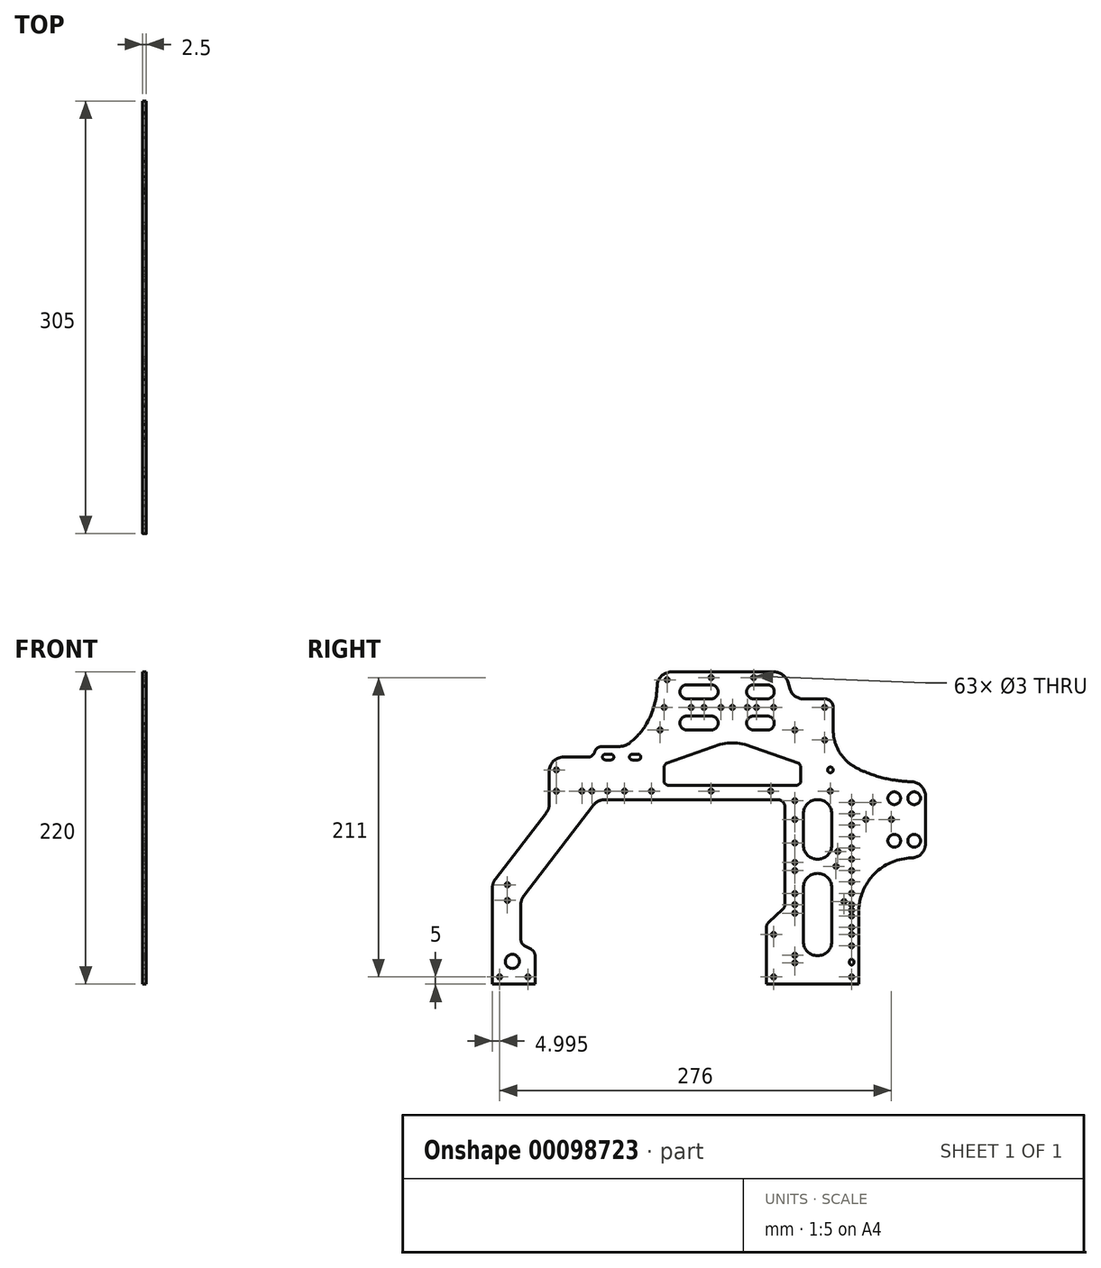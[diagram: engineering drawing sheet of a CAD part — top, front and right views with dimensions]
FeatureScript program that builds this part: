
annotation { "Feature Type Name" : "Feature", "Feature Type Description" : "" }
export const myFeature = defineFeature(function(context is Context, id is Id, definition is map)
    precondition{}
    {
        {
            var Q0;
            Q0=qCreatedBy(makeId("Right.planeOp"),FACE);
            var sketch = newSketch(context, id + "F0", { "sketchPlane" : qUnion([Q0])});
            skLineSegment(sketch, "E0", {"start": v(13.27, 60) * mm, "end": v(19.72, 60) * mm});
            skLineSegment(sketch, "E1", {"start": v(19.72, 60) * mm, "end": v(25.1, 59.07) * mm});
            skLineSegment(sketch, "E2", {"start": v(25.1, 59.07) * mm, "end": v(63.17, 45.47) * mm});
            skLineSegment(sketch, "E3", {"start": v(63.17, 45.47) * mm, "end": v(64.5, 43.6) * mm});
            skLineSegment(sketch, "E4", {"start": v(64.5, 43.6) * mm, "end": v(64.5, 32) * mm});
            skLineSegment(sketch, "E5", {"start": v(64.5, 32) * mm, "end": v(62.5, 30) * mm});
            skLineSegment(sketch, "E6", {"start": v(62.5, 30) * mm, "end": v(-29.5, 30) * mm});
            skLineSegment(sketch, "E7", {"start": v(-29.5, 30) * mm, "end": v(-31.5, 32) * mm});
            skLineSegment(sketch, "E8", {"start": v(-31.5, 32) * mm, "end": v(-31.5, 43.6) * mm});
            skLineSegment(sketch, "E9", {"start": v(-31.5, 43.6) * mm, "end": v(-30.18, 45.47) * mm});
            skLineSegment(sketch, "E10", {"start": v(-30.18, 45.47) * mm, "end": v(7.89, 59.07) * mm});
            skLineSegment(sketch, "E11", {"start": v(7.89, 59.07) * mm, "end": v(13.27, 60) * mm});
            skCircle(sketch, "E12", {"center": v(-138.5, -94) * mm, "radius": 5 * mm});
            skCircle(sketch, "E13", {"center": v(-147.5, -105) * mm, "radius": 1.5 * mm});
            skCircle(sketch, "E14", {"center": v(-127.5, -105) * mm, "radius": 1.5 * mm});
            skCircle(sketch, "E15", {"center": v(-142, -51) * mm, "radius": 1.5 * mm});
            skCircle(sketch, "E16", {"center": v(-142, -40) * mm, "radius": 1.5 * mm});
            skCircle(sketch, "E17", {"center": v(-107.5, 26) * mm, "radius": 1.5 * mm});
            skCircle(sketch, "E18", {"center": v(-107.5, 41) * mm, "radius": 1.5 * mm});
            skCircle(sketch, "E19", {"center": v(-89.5, 26) * mm, "radius": 1.5 * mm});
            skCircle(sketch, "E20", {"center": v(-82.5, 26) * mm, "radius": 1.5 * mm});
            skCircle(sketch, "E21", {"center": v(-71.5, 26) * mm, "radius": 1.5 * mm});
            skArc(sketch, "E22", {"start": v(-75, 50) * mm, "mid": v(-74.42, 48.59) * mm, "end": v(-73, 48) * mm});
            skLineSegment(sketch, "E23", {"start": v(-73, 48) * mm, "end": v(-69, 48) * mm});
            skArc(sketch, "E24", {"start": v(-69, 48) * mm, "mid": v(-67.6, 48.59) * mm, "end": v(-67, 50) * mm});
            skArc(sketch, "E25", {"start": v(-67, 50) * mm, "mid": v(-67.6, 51.41) * mm, "end": v(-69, 52) * mm});
            skLineSegment(sketch, "E26", {"start": v(-69, 52) * mm, "end": v(-73, 52) * mm});
            skArc(sketch, "E27", {"start": v(-73, 52) * mm, "mid": v(-74.42, 51.41) * mm, "end": v(-75, 50) * mm});
            skArc(sketch, "E28", {"start": v(-56, 50) * mm, "mid": v(-55.42, 48.59) * mm, "end": v(-54, 48) * mm});
            skLineSegment(sketch, "E29", {"start": v(-54, 48) * mm, "end": v(-50, 48) * mm});
            skArc(sketch, "E30", {"start": v(-50, 48) * mm, "mid": v(-48.6, 48.59) * mm, "end": v(-48, 50) * mm});
            skArc(sketch, "E31", {"start": v(-48, 50) * mm, "mid": v(-48.6, 51.41) * mm, "end": v(-50, 52) * mm});
            skLineSegment(sketch, "E32", {"start": v(-50, 52) * mm, "end": v(-54, 52) * mm});
            skArc(sketch, "E33", {"start": v(-54, 52) * mm, "mid": v(-55.42, 51.41) * mm, "end": v(-56, 50) * mm});
            skCircle(sketch, "E34", {"center": v(-40.5, 26) * mm, "radius": 1.5 * mm});
            skCircle(sketch, "E35", {"center": v(1.5, 26) * mm, "radius": 1.5 * mm});
            skCircle(sketch, "E36", {"center": v(43.5, 26) * mm, "radius": 1.5 * mm});
            skCircle(sketch, "E37", {"center": v(60.5, 6) * mm, "radius": 1.5 * mm});
            skCircle(sketch, "E38", {"center": v(60.5, -10.5) * mm, "radius": 1.5 * mm});
            skLineSegment(sketch, "E39", {"start": v(66.5, 10) * mm, "end": v(66.5, -12) * mm});
            skArc(sketch, "E40", {"start": v(66.5, -12) * mm, "mid": v(69.42, -19.07) * mm, "end": v(76.5, -22) * mm});
            skArc(sketch, "E41", {"start": v(76.5, -22) * mm, "mid": v(83.57, -19.07) * mm, "end": v(86.5, -12) * mm});
            skLineSegment(sketch, "E42", {"start": v(86.5, -12) * mm, "end": v(86.5, 10) * mm});
            skArc(sketch, "E43", {"start": v(86.5, 10) * mm, "mid": v(83.57, 17.07) * mm, "end": v(76.5, 20) * mm});
            skArc(sketch, "E44", {"start": v(76.5, 20) * mm, "mid": v(69.42, 17.07) * mm, "end": v(66.5, 10) * mm});
            skLineSegment(sketch, "E45", {"start": v(66.5, -42) * mm, "end": v(66.5, -80) * mm});
            skArc(sketch, "E46", {"start": v(66.5, -80) * mm, "mid": v(69.42, -87.07) * mm, "end": v(76.5, -90) * mm});
            skArc(sketch, "E47", {"start": v(76.5, -90) * mm, "mid": v(83.57, -87.07) * mm, "end": v(86.5, -80) * mm});
            skLineSegment(sketch, "E48", {"start": v(86.5, -80) * mm, "end": v(86.5, -42) * mm});
            skArc(sketch, "E49", {"start": v(86.5, -42) * mm, "mid": v(83.57, -34.93) * mm, "end": v(76.5, -32) * mm});
            skArc(sketch, "E50", {"start": v(76.5, -32) * mm, "mid": v(69.42, -34.93) * mm, "end": v(66.5, -42) * mm});
            skCircle(sketch, "E51", {"center": v(130.5, -9) * mm, "radius": 4.5 * mm});
            skCircle(sketch, "E52", {"center": v(144.5, -9) * mm, "radius": 4.5 * mm});
            skCircle(sketch, "E53", {"center": v(130.5, 21) * mm, "radius": 4.5 * mm});
            skCircle(sketch, "E54", {"center": v(144.5, 21) * mm, "radius": 4.5 * mm});
            skArc(sketch, "E55", {"start": v(-20.5, 74) * mm, "mid": v(-19.04, 70.46) * mm, "end": v(-15.5, 69) * mm});
            skLineSegment(sketch, "E56", {"start": v(-15.5, 69) * mm, "end": v(1.5, 69) * mm});
            skArc(sketch, "E57", {"start": v(1.5, 69) * mm, "mid": v(5.03, 70.46) * mm, "end": v(6.5, 74) * mm});
            skArc(sketch, "E58", {"start": v(6.5, 74) * mm, "mid": v(5.03, 77.54) * mm, "end": v(1.5, 79) * mm});
            skLineSegment(sketch, "E59", {"start": v(1.5, 79) * mm, "end": v(-15.5, 79) * mm});
            skArc(sketch, "E60", {"start": v(-15.5, 79) * mm, "mid": v(-19.04, 77.54) * mm, "end": v(-20.5, 74) * mm});
            skArc(sketch, "E61", {"start": v(-20.5, 96) * mm, "mid": v(-19.04, 92.46) * mm, "end": v(-15.5, 91) * mm});
            skLineSegment(sketch, "E62", {"start": v(-15.5, 91) * mm, "end": v(1.5, 91) * mm});
            skArc(sketch, "E63", {"start": v(1.5, 91) * mm, "mid": v(5.03, 92.46) * mm, "end": v(6.5, 96) * mm});
            skArc(sketch, "E64", {"start": v(6.5, 96) * mm, "mid": v(5.03, 99.54) * mm, "end": v(1.5, 101) * mm});
            skLineSegment(sketch, "E65", {"start": v(1.5, 101) * mm, "end": v(-15.5, 101) * mm});
            skArc(sketch, "E66", {"start": v(-15.5, 101) * mm, "mid": v(-19.04, 99.54) * mm, "end": v(-20.5, 96) * mm});
            skArc(sketch, "E67", {"start": v(26.5, 96) * mm, "mid": v(27.96, 92.46) * mm, "end": v(31.5, 91) * mm});
            skLineSegment(sketch, "E68", {"start": v(31.5, 91) * mm, "end": v(41, 91) * mm});
            skArc(sketch, "E69", {"start": v(41, 91) * mm, "mid": v(44.53, 92.46) * mm, "end": v(46, 96) * mm});
            skArc(sketch, "E70", {"start": v(46, 96) * mm, "mid": v(44.53, 99.54) * mm, "end": v(41, 101) * mm});
            skLineSegment(sketch, "E71", {"start": v(41, 101) * mm, "end": v(31.5, 101) * mm});
            skArc(sketch, "E72", {"start": v(31.5, 101) * mm, "mid": v(27.96, 99.54) * mm, "end": v(26.5, 96) * mm});
            skArc(sketch, "E73", {"start": v(26.5, 74) * mm, "mid": v(27.96, 70.46) * mm, "end": v(31.5, 69) * mm});
            skLineSegment(sketch, "E74", {"start": v(31.5, 69) * mm, "end": v(41, 69) * mm});
            skArc(sketch, "E75", {"start": v(41, 69) * mm, "mid": v(44.53, 70.46) * mm, "end": v(46, 74) * mm});
            skArc(sketch, "E76", {"start": v(46, 74) * mm, "mid": v(44.53, 77.54) * mm, "end": v(41, 79) * mm});
            skLineSegment(sketch, "E77", {"start": v(41, 79) * mm, "end": v(31.5, 79) * mm});
            skArc(sketch, "E78", {"start": v(31.5, 79) * mm, "mid": v(27.96, 77.54) * mm, "end": v(26.5, 74) * mm});
            skCircle(sketch, "E79", {"center": v(-34.5, 69) * mm, "radius": 1.5 * mm});
            skCircle(sketch, "E80", {"center": v(-31.5, 85) * mm, "radius": 1.5 * mm});
            skCircle(sketch, "E81", {"center": v(-29.5, 104.5) * mm, "radius": 1.5 * mm});
            skCircle(sketch, "E82", {"center": v(-12.5, 85) * mm, "radius": 1.5 * mm});
            skCircle(sketch, "E83", {"center": v(-3.5, 85) * mm, "radius": 1.5 * mm});
            skCircle(sketch, "E84", {"center": v(8.5, 85) * mm, "radius": 1.5 * mm});
            skCircle(sketch, "E85", {"center": v(16.5, 85) * mm, "radius": 1.5 * mm});
            skCircle(sketch, "E86", {"center": v(27, 85) * mm, "radius": 1.5 * mm});
            skCircle(sketch, "E87", {"center": v(33.5, 85) * mm, "radius": 1.5 * mm});
            skCircle(sketch, "E88", {"center": v(45.5, 85) * mm, "radius": 1.5 * mm});
            skCircle(sketch, "E89", {"center": v(1.5, 106) * mm, "radius": 1.5 * mm});
            skCircle(sketch, "E90", {"center": v(31.5, 106) * mm, "radius": 1.5 * mm});
            skCircle(sketch, "E91", {"center": v(81.5, 85) * mm, "radius": 1.5 * mm});
            skCircle(sketch, "E92", {"center": v(60.5, 69) * mm, "radius": 1.5 * mm});
            skCircle(sketch, "E93", {"center": v(60.5, -24.25) * mm, "radius": 1.5 * mm});
            skCircle(sketch, "E94", {"center": v(60.5, -30) * mm, "radius": 1.5 * mm});
            skCircle(sketch, "E95", {"center": v(60.5, 19.25) * mm, "radius": 1.5 * mm});
            skCircle(sketch, "E96", {"center": v(60.5, -46.25) * mm, "radius": 1.5 * mm});
            skCircle(sketch, "E97", {"center": v(60.5, -54) * mm, "radius": 1.5 * mm});
            skCircle(sketch, "E98", {"center": v(60.5, -60) * mm, "radius": 1.5 * mm});
            skCircle(sketch, "E99", {"center": v(45.5, -75) * mm, "radius": 1.5 * mm});
            skCircle(sketch, "E100", {"center": v(45.5, -105) * mm, "radius": 1.5 * mm});
            skCircle(sketch, "E101", {"center": v(60.5, -89.75) * mm, "radius": 1.5 * mm});
            skCircle(sketch, "E102", {"center": v(60.5, -95) * mm, "radius": 1.5 * mm});
            skCircle(sketch, "E103", {"center": v(100.5, -105) * mm, "radius": 1.5 * mm});
            skCircle(sketch, "E104", {"center": v(85.5, 26) * mm, "radius": 1.5 * mm});
            skCircle(sketch, "E105", {"center": v(85.5, 41) * mm, "radius": 2 * mm});
            skCircle(sketch, "E106", {"center": v(100.5, 18) * mm, "radius": 1.5 * mm});
            skCircle(sketch, "E107", {"center": v(100.5, 10) * mm, "radius": 1.5 * mm});
            skCircle(sketch, "E108", {"center": v(100.5, 2) * mm, "radius": 1.5 * mm});
            skCircle(sketch, "E109", {"center": v(110.5, 6) * mm, "radius": 1.5 * mm});
            skCircle(sketch, "E110", {"center": v(115.5, 18) * mm, "radius": 1.5 * mm});
            skCircle(sketch, "E111", {"center": v(128.5, 6) * mm, "radius": 1.5 * mm});
            skCircle(sketch, "E112", {"center": v(100.5, -6) * mm, "radius": 1.5 * mm});
            skCircle(sketch, "E113", {"center": v(100.5, -14) * mm, "radius": 1.5 * mm});
            skCircle(sketch, "E114", {"center": v(90.75, -16.5) * mm, "radius": 1.5 * mm});
            skCircle(sketch, "E115", {"center": v(89.5, -27) * mm, "radius": 1.5 * mm});
            skCircle(sketch, "E116", {"center": v(100.5, -22) * mm, "radius": 1.5 * mm});
            skCircle(sketch, "E117", {"center": v(100.5, -30) * mm, "radius": 1.5 * mm});
            skCircle(sketch, "E118", {"center": v(100.5, -38) * mm, "radius": 1.5 * mm});
            skCircle(sketch, "E119", {"center": v(100.5, -54) * mm, "radius": 1.5 * mm});
            skCircle(sketch, "E120", {"center": v(95.12, -51.87) * mm, "radius": 1.5 * mm});
            skCircle(sketch, "E121", {"center": v(100.5, -46) * mm, "radius": 1.5 * mm});
            skCircle(sketch, "E122", {"center": v(100.5, -58) * mm, "radius": 1.5 * mm});
            skCircle(sketch, "E123", {"center": v(100.5, -62) * mm, "radius": 1.5 * mm});
            skCircle(sketch, "E124", {"center": v(100.5, -70) * mm, "radius": 1.5 * mm});
            skCircle(sketch, "E125", {"center": v(100.5, -75) * mm, "radius": 1.5 * mm});
            skCircle(sketch, "E126", {"center": v(100.5, -83) * mm, "radius": 1.5 * mm});
            skLineSegment(sketch, "E127", {"start": v(99, -94) * mm, "end": v(99, -95) * mm});
            skArc(sketch, "E128", {"start": v(99, -95) * mm, "mid": v(99.43, -96.06) * mm, "end": v(100.5, -96.5) * mm});
            skArc(sketch, "E129", {"start": v(100.5, -96.5) * mm, "mid": v(101.56, -96.06) * mm, "end": v(102, -95) * mm});
            skLineSegment(sketch, "E130", {"start": v(102, -95) * mm, "end": v(102, -94) * mm});
            skArc(sketch, "E131", {"start": v(102, -94) * mm, "mid": v(101.56, -92.94) * mm, "end": v(100.5, -92.5) * mm});
            skArc(sketch, "E132", {"start": v(100.5, -92.5) * mm, "mid": v(99.43, -92.94) * mm, "end": v(99, -94) * mm});
            skLineSegment(sketch, "E133", {"start": v(105.5, -58) * mm, "end": v(105.5, -110) * mm});
            skLineSegment(sketch, "E134", {"start": v(105.5, -110) * mm, "end": v(40.5, -110) * mm});
            skLineSegment(sketch, "E135", {"start": v(40.5, -110) * mm, "end": v(40.5, -70.03) * mm});
            skArc(sketch, "E136", {"start": v(40.5, -70.03) * mm, "mid": v(40.92, -68.02) * mm, "end": v(42.11, -66.35) * mm});
            skLineSegment(sketch, "E137", {"start": v(42.11, -66.35) * mm, "end": v(51.88, -57.39) * mm});
            skArc(sketch, "E138", {"start": v(51.88, -57.39) * mm, "mid": v(53.07, -55.71) * mm, "end": v(53.5, -53.7) * mm});
            skLineSegment(sketch, "E139", {"start": v(53.5, -53.7) * mm, "end": v(53.5, 15) * mm});
            skArc(sketch, "E140", {"start": v(53.5, 15) * mm, "mid": v(52.03, 18.54) * mm, "end": v(48.5, 20) * mm});
            skLineSegment(sketch, "E141", {"start": v(48.5, 20) * mm, "end": v(-73.57, 20) * mm});
            skArc(sketch, "E142", {"start": v(-73.57, 20) * mm, "mid": v(-78, 18.97) * mm, "end": v(-81.5, 16.08) * mm});
            skLineSegment(sketch, "E143", {"start": v(-81.5, 16.08) * mm, "end": v(-130.44, -47.8) * mm});
            skArc(sketch, "E144", {"start": v(-130.44, -47.8) * mm, "mid": v(-131.98, -50.68) * mm, "end": v(-132.5, -53.89) * mm});
            skLineSegment(sketch, "E145", {"start": v(-132.5, -53.89) * mm, "end": v(-132.5, -78.54) * mm});
            skArc(sketch, "E146", {"start": v(-132.5, -78.54) * mm, "mid": v(-131.8, -81.09) * mm, "end": v(-129.91, -82.92) * mm});
            skLineSegment(sketch, "E147", {"start": v(-129.91, -82.92) * mm, "end": v(-125.1, -85.58) * mm});
            skArc(sketch, "E148", {"start": v(-125.1, -85.58) * mm, "mid": v(-123.2, -87.41) * mm, "end": v(-122.5, -89.96) * mm});
            skLineSegment(sketch, "E149", {"start": v(-122.5, -89.96) * mm, "end": v(-122.5, -110) * mm});
            skLineSegment(sketch, "E150", {"start": v(-122.5, -110) * mm, "end": v(-152.5, -110) * mm});
            skLineSegment(sketch, "E151", {"start": v(-152.5, -110) * mm, "end": v(-152.5, -42.06) * mm});
            skArc(sketch, "E152", {"start": v(-152.5, -42.06) * mm, "mid": v(-151.97, -38.85) * mm, "end": v(-150.44, -35.97) * mm});
            skLineSegment(sketch, "E153", {"start": v(-150.44, -35.97) * mm, "end": v(-114.57, 10.8) * mm});
            skArc(sketch, "E154", {"start": v(-114.57, 10.8) * mm, "mid": v(-113.03, 13.68) * mm, "end": v(-112.5, 16.9) * mm});
            skLineSegment(sketch, "E155", {"start": v(-112.5, 16.9) * mm, "end": v(-112.5, 40) * mm});
            skArc(sketch, "E156", {"start": v(-112.5, 40) * mm, "mid": v(-109.58, 47.07) * mm, "end": v(-102.5, 50) * mm});
            skLineSegment(sketch, "E157", {"start": v(-102.5, 50) * mm, "end": v(-85.5, 50) * mm});
            skArc(sketch, "E158", {"start": v(-85.5, 50) * mm, "mid": v(-82.31, 50.95) * mm, "end": v(-80.5, 53.75) * mm});
            skArc(sketch, "E159", {"start": v(-80.5, 53.75) * mm, "mid": v(-78.6, 56.43) * mm, "end": v(-75.5, 57.5) * mm});
            skLineSegment(sketch, "E160", {"start": v(-75.5, 57.5) * mm, "end": v(-62.5, 57.5) * mm});
            skArc(sketch, "E161", {"start": v(-62.5, 57.5) * mm, "mid": v(-58.45, 58.42) * mm, "end": v(-55, 60.75) * mm});
            skArc(sketch, "E162", {"start": v(-55, 60.75) * mm, "mid": v(-48.87, 66.57) * mm, "end": v(-44, 73.5) * mm});
            skArc(sketch, "E163", {"start": v(-44, 73.5) * mm, "mid": v(-38.59, 86.28) * mm, "end": v(-36.5, 100) * mm});
            skArc(sketch, "E164", {"start": v(-36.5, 100) * mm, "mid": v(-33.58, 107.07) * mm, "end": v(-26.5, 110) * mm});
            skLineSegment(sketch, "E165", {"start": v(-26.5, 110) * mm, "end": v(-2, 110) * mm});
            skLineSegment(sketch, "E166", {"start": v(-2, 110) * mm, "end": v(45.98, 110) * mm});
            skArc(sketch, "E167", {"start": v(45.98, 110) * mm, "mid": v(51.99, 108) * mm, "end": v(55.59, 102.78) * mm});
            skLineSegment(sketch, "E168", {"start": v(55.59, 102.78) * mm, "end": v(56.9, 98.22) * mm});
            skArc(sketch, "E169", {"start": v(56.9, 98.22) * mm, "mid": v(60.5, 93) * mm, "end": v(66.51, 91) * mm});
            skLineSegment(sketch, "E170", {"start": v(66.51, 91) * mm, "end": v(72.5, 91) * mm});
            skLineSegment(sketch, "E171", {"start": v(72.5, 91) * mm, "end": v(81.5, 91) * mm});
            skArc(sketch, "E172", {"start": v(81.5, 91) * mm, "mid": v(85.74, 89.24) * mm, "end": v(87.5, 85) * mm});
            skLineSegment(sketch, "E173", {"start": v(87.5, 85) * mm, "end": v(87.5, 68) * mm});
            skArc(sketch, "E174", {"start": v(87.5, 68) * mm, "mid": v(88.4, 61.85) * mm, "end": v(90.5, 56) * mm});
            skArc(sketch, "E175", {"start": v(90.5, 56) * mm, "mid": v(94.17, 50.28) * mm, "end": v(99, 45.5) * mm});
            skArc(sketch, "E176", {"start": v(99, 45.5) * mm, "mid": v(104.4, 42.07) * mm, "end": v(110.25, 39.5) * mm});
            skArc(sketch, "E177", {"start": v(110.25, 39.5) * mm, "mid": v(119.46, 36.21) * mm, "end": v(129, 34) * mm});
            skArc(sketch, "E178", {"start": v(129, 34) * mm, "mid": v(136.47, 33) * mm, "end": v(144, 32.5) * mm});
            skArc(sketch, "E179", {"start": v(144, 32.5) * mm, "mid": v(149.9, 29.23) * mm, "end": v(152.5, 23) * mm});
            skLineSegment(sketch, "E180", {"start": v(152.5, 23) * mm, "end": v(152.5, -10.75) * mm});
            skArc(sketch, "E181", {"start": v(152.5, -10.75) * mm, "mid": v(149.71, -18.04) * mm, "end": v(142.5, -21) * mm});
            skArc(sketch, "E182", {"start": v(142.5, -21) * mm, "mid": v(129.43, -23.82) * mm, "end": v(118, -30.75) * mm});
            skArc(sketch, "E183", {"start": v(118, -30.75) * mm, "mid": v(110.83, -39.67) * mm, "end": v(106.5, -50.25) * mm});
            skArc(sketch, "E184", {"start": v(106.5, -50.25) * mm, "mid": v(105.82, -54.1) * mm, "end": v(105.5, -58) * mm});
            skCircle(sketch, "E185", {"center": v(81.5, 62) * mm, "radius": 1.5 * mm});
            skCircle(sketch, "E186", {"center": v(-59.5, 26) * mm, "radius": 1.5 * mm});
            skSolve(sketch);
        }
        {
            var Q0;
            Q0=makeQuery(id+"F0.imprint","IMPRINT",FACE,{"disambiguationData":[TD([[makeQuery(id+"F0.imprint","IMPRINT",EDGE,{"derivedFrom":sQuery(id+"F0.wireOp",EDGE,"E0")}),1.0]])]});
            extrude(context, id + "F1", {"entities" : qUnion([Q0]), "depth" : 2.5 * mm, "symmetric" : true});
        }
    });
